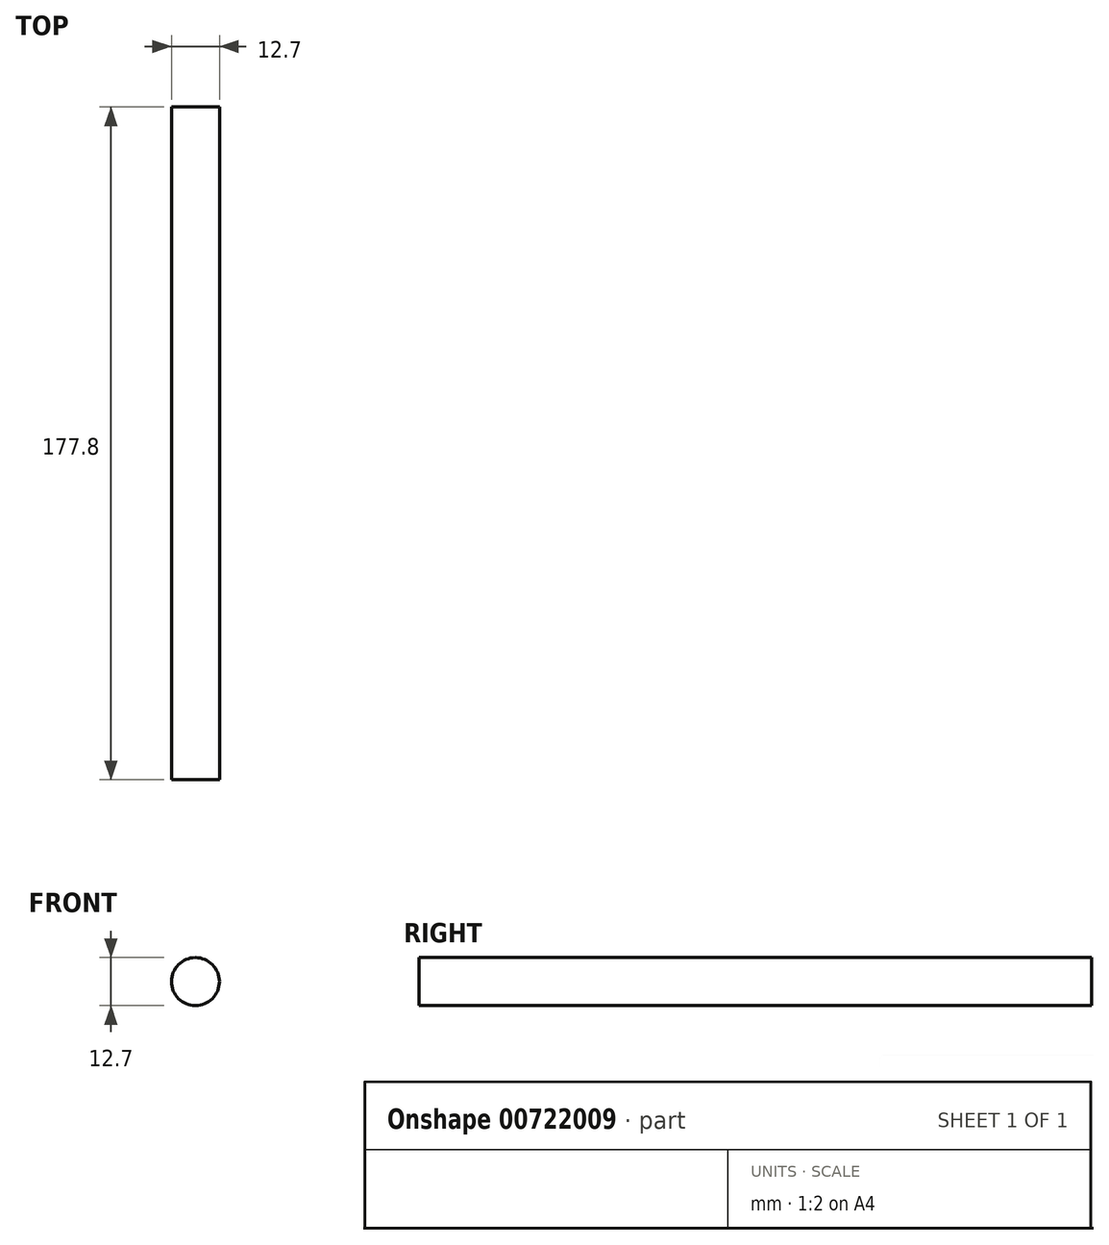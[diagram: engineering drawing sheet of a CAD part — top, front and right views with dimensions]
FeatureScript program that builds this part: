
annotation { "Feature Type Name" : "Feature", "Feature Type Description" : "" }
export const myFeature = defineFeature(function(context is Context, id is Id, definition is map)
    precondition{}
    {
        {
            var Q0;
            Q0=qCreatedBy(makeId("Front.planeOp"),FACE);
            var sketch = newSketch(context, id + "F0", { "sketchPlane" : qUnion([Q0])});
            skCircle(sketch, "E0", {"center": v(0, 0) * mm, "radius": 6.35 * mm});
            skSolve(sketch);
        }
        {
            var Q0;
            Q0=makeQuery(id+"F0.imprint","IMPRINT",FACE,{"disambiguationData":[TD([[makeQuery(id+"F0.imprint","IMPRINT",EDGE,{"derivedFrom":sQuery(id+"F0.wireOp",EDGE,"E0")}),1.0]])]});
            extrude(context, id + "F1", {"entities" : qUnion([Q0]), "depth" : 177.8 * mm, "offsetDistance" : 25.4 * mm});
        }
    });
